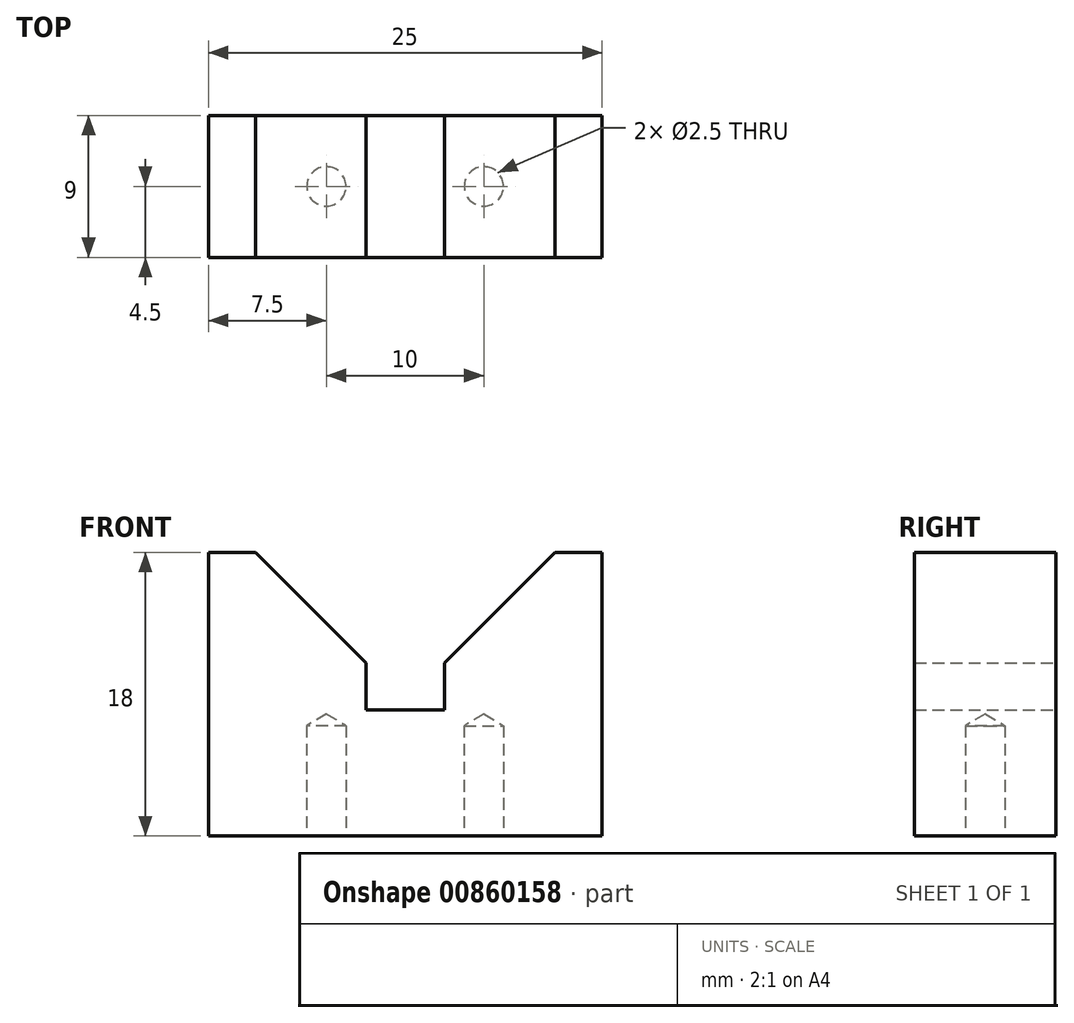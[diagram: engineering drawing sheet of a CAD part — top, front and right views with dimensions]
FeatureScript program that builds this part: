
annotation { "Feature Type Name" : "Feature", "Feature Type Description" : "" }
export const myFeature = defineFeature(function(context is Context, id is Id, definition is map)
    precondition{}
    {
        {
            var Q0;
            Q0=qCreatedBy(makeId("Front.planeOp"),FACE);
            var sketch = newSketch(context, id + "F0", { "sketchPlane" : qUnion([Q0])});
            skLineSegment(sketch, "E0", {"start": v(0, 0) * mm, "end": v(0, 8) * mm});
            skLineSegment(sketch, "E1", {"start": v(0, 8) * mm, "end": v(2.5, 8) * mm});
            skLineSegment(sketch, "E2", {"start": v(2.5, 8) * mm, "end": v(2.5, 11) * mm});
            skLineSegment(sketch, "E3", {"start": v(2.5, 11) * mm, "end": v(9.5, 18) * mm});
            skLineSegment(sketch, "E4", {"start": v(9.5, 18) * mm, "end": v(12.5, 18) * mm});
            skLineSegment(sketch, "E5", {"start": v(12.5, 18) * mm, "end": v(12.5, 0) * mm});
            skLineSegment(sketch, "E6", {"start": v(12.5, 0) * mm, "end": v(0, 0) * mm});
            skSolve(sketch);
        }
        {
            var Q0;
            Q0=makeQuery(id+"F0.imprint","IMPRINT",FACE,{"disambiguationData":[TD([[makeQuery(id+"F0.imprint","IMPRINT",EDGE,{"derivedFrom":sQuery(id+"F0.wireOp",EDGE,"E0")}),-1.0]])]});
            extrude(context, id + "F1", {"entities" : qUnion([Q0]), "endBound" : BoundingType.SYMMETRIC, "depth" : 9 * mm, "offsetDistance" : 25 * mm});
        }
        {
            var Q0;
            Q0=makeQuery(id+"F1.opExtrude","SWEPT_FACE",FACE,{"disambiguationData":[OSD([sQuery(id+"F0.wireOp",EDGE,"E6")])]});
            var sketch = newSketch(context, id + "F2", { "sketchPlane" : qUnion([Q0])});
            skPoint(sketch, "E7", {"position": v(5, 0) * mm});
            skSolve(sketch);
        }
        {
            var Q0;
            Q0=sQuery(id+"F2.wireOp",VERTEX,"E7");
            var Q1;
            Q1=makeQuery(id+"F1.opExtrude","SWEPT_BODY",BODY,{"disambiguationData":[OSD([sQuery(id+"F0.wireOp",EDGE,"E0"),sQuery(id+"F0.wireOp",EDGE,"E1"),sQuery(id+"F0.wireOp",EDGE,"E2"),sQuery(id+"F0.wireOp",EDGE,"E3"),sQuery(id+"F0.wireOp",EDGE,"E4"),sQuery(id+"F0.wireOp",EDGE,"E5"),sQuery(id+"F0.wireOp",EDGE,"E6")])]});
            hole(context, id + "F3", {"style" : HoleStyle.SIMPLE, "endStyle" : HoleEndStyle.BLIND, "standardTappedOrClearance" : lookupTablePath({ "standard" : "ISO", "engagement" : "75%", "pitch" : "0.5 mm", "size" : "M3", "type" : "Tapped" }), "standardBlindInLast" : lookupTablePath({ "standard" : "ISO", "engagement" : "75%", "pitch" : "0.5 mm", "size" : "M3", "type" : "Tapped" }), "holeDiameter" : 2.5 * mm, "majorDiameter" : 3 * mm, "showTappedDepth" : true, "holeDepth" : 7 * mm, "isTappedThrough" : true, "tappedDepth" : 7 * mm, "tapClearance" : 0, "startFromSketch" : true, "locations" : qUnion([Q0]), "scope" : qUnion([Q1])});
        }
        {
            var Q0;
            Q0=makeQuery(id+"F1.opExtrude","SWEPT_BODY",BODY,{"disambiguationData":[OSD([sQuery(id+"F0.wireOp",EDGE,"E0"),sQuery(id+"F0.wireOp",EDGE,"E1"),sQuery(id+"F0.wireOp",EDGE,"E2"),sQuery(id+"F0.wireOp",EDGE,"E3"),sQuery(id+"F0.wireOp",EDGE,"E4"),sQuery(id+"F0.wireOp",EDGE,"E5"),sQuery(id+"F0.wireOp",EDGE,"E6")])]});
            var Q1;
            Q1=qCreatedBy(makeId("Right.planeOp"),FACE);
            mirror(context, id + "F4", {"operationType" : NewBodyOperationType.ADD, "entities" : qUnion([Q0]), "mirrorPlane" : qUnion([Q1])});
        }
    });
